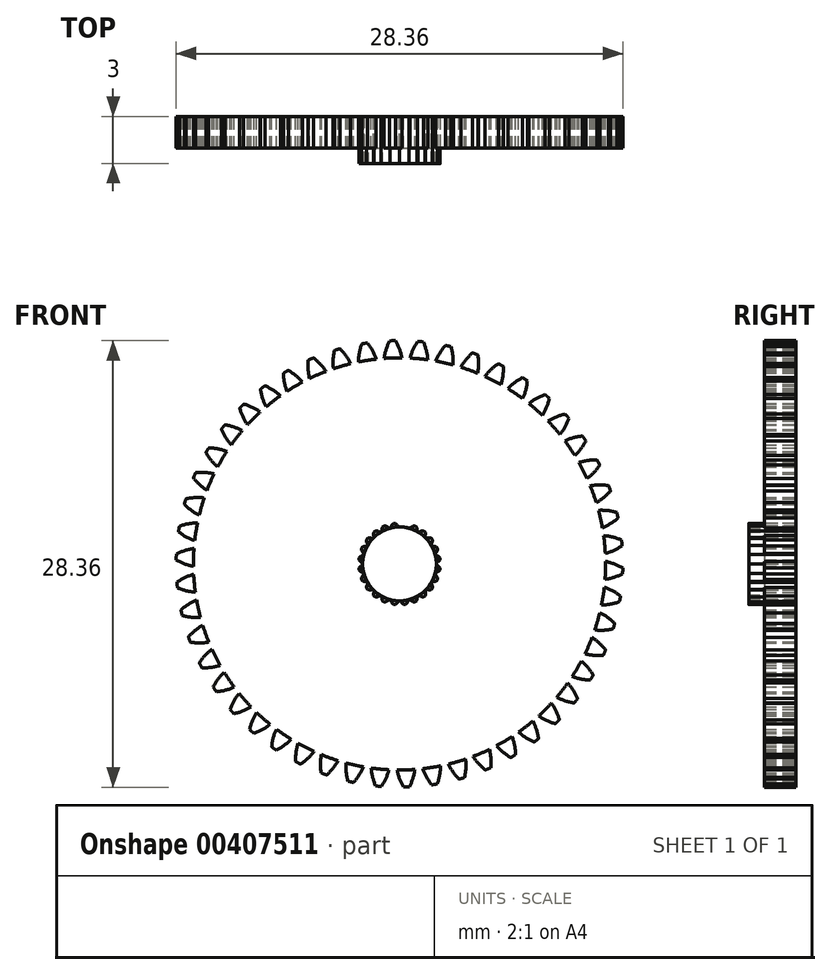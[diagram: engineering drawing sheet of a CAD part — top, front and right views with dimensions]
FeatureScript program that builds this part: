
annotation { "Feature Type Name" : "Feature", "Feature Type Description" : "" }
export const myFeature = defineFeature(function(context is Context, id is Id, definition is map)
    precondition{}
    {
        {
            var Q0;
            Q0=qCreatedBy(makeId("Front.planeOp"),FACE);
            var sketch = newSketch(context, id + "F0", { "sketchPlane" : qUnion([Q0])});
            skCircle(sketch, "E0", {"center": v(0, 0) * mm, "radius": 13.1 * mm});
            skCircle(sketch, "E1", {"center": v(0, 0) * mm, "radius": 13.63 * mm, "construction": true});
            skCircle(sketch, "E2", {"center": v(0, 0) * mm, "radius": 14.18 * mm, "construction": true});
            skLineSegment(sketch, "E3", {"start": v(0, 0) * mm, "end": v(0, 16.85) * mm, "construction": true});
            skLineSegment(sketch, "E4", {"start": v(0, 0) * mm, "end": v(-0.87, 27.82) * mm, "construction": true});
            skLineSegment(sketch, "E5", {"start": v(0, 13.64) * mm, "end": v(-5.77, 13.64) * mm, "construction": true});
            skLineSegment(sketch, "E6", {"start": v(0, 13.64) * mm, "end": v(-5.6, 11.6) * mm, "construction": true});
            skCircle(sketch, "E7", {"center": v(0, 0) * mm, "radius": 12.81 * mm, "construction": true});
            skCircle(sketch, "E8", {"center": v(0, 13.64) * mm, "radius": 3.41 * mm, "construction": true});
            skCircle(sketch, "E9", {"center": v(-3.18, 12.41) * mm, "radius": 3.41 * mm, "construction": true});
            skArc(sketch, "E10", {"start": v(0.16, 13.09) * mm, "mid": v(0, 13.65) * mm, "end": v(-0.26, 14.18) * mm});
            skArc(sketch, "E11.MirrorCS", {"start": v(-0.98, 13.05) * mm, "mid": v(-0.85, 13.62) * mm, "end": v(-0.63, 14.17) * mm});
            skArc(sketch, "E12", {"start": v(-0.26, 14.18) * mm, "mid": v(-0.45, 14.18) * mm, "end": v(-0.63, 14.17) * mm});
            skLineSegment(sketch, "E13", {"start": v(0.16, 13.09) * mm, "end": v(0.16, 13.09) * mm});
            skLineSegment(sketch, "E14", {"start": v(0.16, 13.09) * mm, "end": v(0.16, 13.08) * mm});
            skLineSegment(sketch, "E15", {"start": v(-0.98, 13.05) * mm, "end": v(-0.98, 13.05) * mm});
            skLineSegment(sketch, "E16", {"start": v(-0.98, 13.04) * mm, "end": v(-0.98, 13.05) * mm});
            skSolve(sketch);
        }
        {
            var Q0;
            {var subQ0=sQuery(id+"F0.wireOp",EDGE,"E10");Q0=makeQuery(id+"F0.imprint","IMPRINT",FACE,{"disambiguationData":[TD([[makeQuery(id+"F0.imprint","IMPRINT",EDGE,{"derivedFrom":subQ0}),1.0]])]});}
            var Q1;
            {var subQ0=sQuery(id+"F0.wireOp",EDGE,"E0");var subQ1=makeQuery(id+"F0.imprint","IMPRINT",VERTEX,{"disambiguationData":[OD(0.0)],"derivedFrom":subQ0});Q1=makeQuery(id+"F0.imprint","IMPRINT",FACE,{"disambiguationData":[TD([[makeQuery(id+"F0.imprint","IMPRINT",EDGE,{"disambiguationData":[TD([[subQ1,-1.0]])],"derivedFrom":subQ0}),1.0]])]});}
            extrude(context, id + "F1", {"entities" : qUnion([Q0, Q1]), "depth" : 2 * mm});
        }
        {
            var Q0;
            Q0=makeQuery(id+"F1.opExtrude","SWEPT_BODY",BODY,{"disambiguationData":[OSD([sQuery(id+"F0.wireOp",EDGE,"E0"),sQuery(id+"F0.wireOp",EDGE,"E10"),sQuery(id+"F0.wireOp",EDGE,"E11.MirrorCS"),sQuery(id+"F0.wireOp",EDGE,"E12")])]});
            var Q1;
            Q1=sQuery(id+"F0.wireOp",EDGE,"E7");
            circularPattern(context, id + "F2", {"operationType" : NewBodyOperationType.ADD, "entities" : qUnion([Q0]), "axis" : qUnion([Q1]), "angle" : 360 * degree, "instanceCount" : 50, "equalSpace" : true});
        }
        {
            var Q0;
            Q0=qCreatedBy(makeId("Front.planeOp"),FACE);
            var sketch = newSketch(context, id + "F3", { "sketchPlane" : qUnion([Q0])});
            skCircle(sketch, "E17", {"center": v(0, 0) * mm, "radius": 2.6 * mm, "construction": true});
            skCircle(sketch, "E18", {"center": v(0, 0) * mm, "radius": 2.35 * mm});
            skLineSegment(sketch, "E19", {"start": v(0, 0) * mm, "end": v(0, 2.26) * mm, "construction": true});
            skLineSegment(sketch, "E20", {"start": v(0, 0) * mm, "end": v(0.61, 2.28) * mm, "construction": true});
            skLineSegment(sketch, "E21", {"start": v(0, 0) * mm, "end": v(0.34, 2.57) * mm, "construction": true});
            skFitSpline(sketch, "E22", {"points": [v(0, 2.35) * mm, v(0.12, 2.46) * mm, v(0.34, 2.58) * mm, v(0.5, 2.43) * mm, v(0.6, 2.27) * mm], "startDerivative": vector(0.95, -0.01) * mm, "endDerivative": vector(1.15, -0.28) * mm});
            skSolve(sketch);
        }
        {
            var Q0;
            Q0 = qSketchRegion(id + "F3", true);
            extrude(context, id + "F4", {"entities" : qUnion([Q0]), "depth" : 3 * mm});
        }
        {
            var Q0;
            Q0=makeQuery(id+"F4.opExtrude","SWEPT_BODY",BODY,{"disambiguationData":[OSD([sQuery(id+"F3.wireOp",EDGE,"E22"),sQuery(id+"F3.wireOp",EDGE,"E18")])]});
            var Q1;
            Q1=makeQuery(id+"F4.opExtrude","SWEPT_FACE",FACE,{"disambiguationData":[OSD([sQuery(id+"F3.wireOp",EDGE,"E18")])]});
            circularPattern(context, id + "F5", {"operationType" : NewBodyOperationType.ADD, "entities" : qUnion([Q0]), "axis" : qUnion([Q1]), "angle" : 360 * degree, "instanceCount" : 24, "equalSpace" : true});
        }
        {
            var Q0;
            Q0=makeQuery(id+"F4.opExtrude","SWEPT_BODY",BODY,{"disambiguationData":[OSD([sQuery(id+"F3.wireOp",EDGE,"E22"),sQuery(id+"F3.wireOp",EDGE,"E18")])]});
            var Q1;
            Q1=makeQuery(id+"F1.opExtrude","SWEPT_BODY",BODY,{"disambiguationData":[OSD([sQuery(id+"F0.wireOp",EDGE,"E0"),sQuery(id+"F0.wireOp",EDGE,"E10"),sQuery(id+"F0.wireOp",EDGE,"E11.MirrorCS"),sQuery(id+"F0.wireOp",EDGE,"E12")])]});
            booleanBodies(context, id + "F6", {"operationType" : BooleanOperationType.SUBTRACTION, "tools" : qUnion([Q0]), "targets" : qUnion([Q1])});
        }
    });
